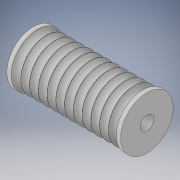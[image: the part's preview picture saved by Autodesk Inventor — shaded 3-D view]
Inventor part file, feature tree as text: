
AUTODESK INVENTOR PART (.ipt)
format: ipt  version: 2018 (Build 220112000, 112)  size: 348,672 bytes
history: native  units: in
note: dims shown in document units (in); Inventor stores cm internally (conversion verified against a paired STEP export)
features: revolve x1, sketch x1
ambient origin geometry x8: Origin, YZ Plane, XZ Plane, XY Plane, X Axis, Y Axis, Z Axis, Center Point
bodies: Body1 (feature_tree)
feature tree (2):
  revolve  "Revolution3"  [1 undecoded]
  sketch  "Sketch1"  dims[d33=0.75in d34=3.25in d35=0.125in d40=0.125in d43=0.125in d44=0.125in d46=0.125in d47=0.125in d56=0.125in d59=0.125in d60=90.0deg d63=0.125in d70=0.125in d71=0.0in d72=0.195in d73=0.125in d75=0.125in d76=0.125in d77=0.025in d78=0.125in d79=90.0deg d81=90.0deg]
note: 1 required parameter value undecoded (feature->parameter linkage not recoverable at this tier; creation-order binding heuristic only, values carry confidence <= 0.55)
